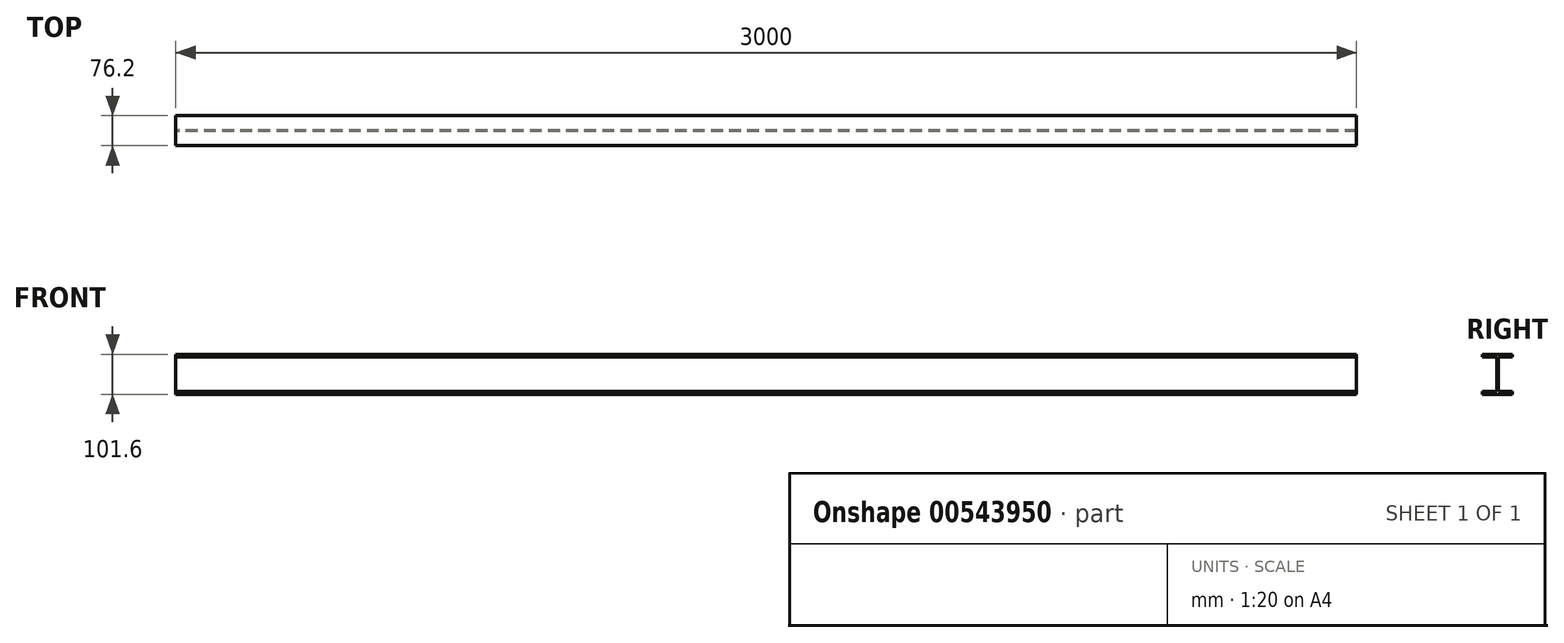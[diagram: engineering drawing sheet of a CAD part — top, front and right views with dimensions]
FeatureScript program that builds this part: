
annotation { "Feature Type Name" : "Feature", "Feature Type Description" : "" }
export const myFeature = defineFeature(function(context is Context, id is Id, definition is map)
    precondition{}
    {
        {
            var Q0;
            Q0=qCreatedBy(makeId("Right.planeOp"),FACE);
            var sketch = newSketch(context, id + "F0", { "sketchPlane" : qUnion([Q0])});
            skLineSegment(sketch, "E0", {"start": v(-38.1, 0) * mm, "end": v(38.1, 0) * mm});
            skLineSegment(sketch, "E1", {"start": v(38.1, 0) * mm, "end": v(38.1, -7.37) * mm});
            skLineSegment(sketch, "E2", {"start": v(38.1, -7.37) * mm, "end": v(2.16, -7.37) * mm});
            skLineSegment(sketch, "E3", {"start": v(2.16, -7.37) * mm, "end": v(2.16, -94.23) * mm});
            skLineSegment(sketch, "E4", {"start": v(2.16, -94.23) * mm, "end": v(38.1, -94.23) * mm});
            skLineSegment(sketch, "E5", {"start": v(38.1, -94.23) * mm, "end": v(38.1, -101.6) * mm});
            skLineSegment(sketch, "E6", {"start": v(38.1, -101.6) * mm, "end": v(-38.1, -101.6) * mm});
            skLineSegment(sketch, "E7", {"start": v(-38.1, -101.6) * mm, "end": v(-38.1, -94.23) * mm});
            skLineSegment(sketch, "E8", {"start": v(-38.1, -94.23) * mm, "end": v(-2.16, -94.23) * mm});
            skLineSegment(sketch, "E9", {"start": v(-2.16, -94.23) * mm, "end": v(-2.16, -7.37) * mm});
            skLineSegment(sketch, "E10", {"start": v(-2.16, -7.37) * mm, "end": v(-38.1, -7.37) * mm});
            skLineSegment(sketch, "E11", {"start": v(-38.1, -7.37) * mm, "end": v(-38.1, 0) * mm});
            skSolve(sketch);
        }
        {
            var Q0;
            Q0=makeQuery(id+"F0.imprint","IMPRINT",FACE,{"disambiguationData":[TD([[makeQuery(id+"F0.imprint","IMPRINT",EDGE,{"derivedFrom":sQuery(id+"F0.wireOp",EDGE,"E0")}),-1.0]])]});
            extrude(context, id + "F1", {"entities" : qUnion([Q0]), "depth" : 3000 * mm, "offsetDistance" : 25 * mm});
        }
    });
